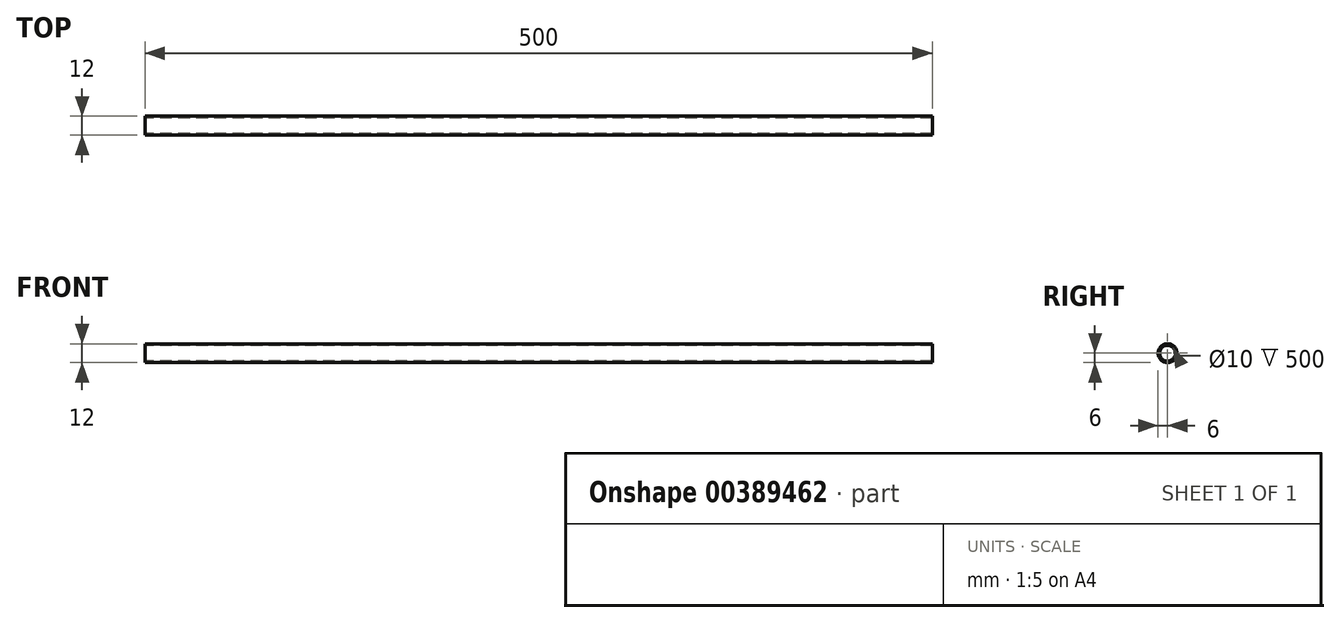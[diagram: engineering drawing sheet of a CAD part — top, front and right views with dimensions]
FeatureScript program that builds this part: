
annotation { "Feature Type Name" : "Feature", "Feature Type Description" : "" }
export const myFeature = defineFeature(function(context is Context, id is Id, definition is map)
    precondition{}
    {
        {
            var Q0;
            Q0=qCreatedBy(makeId("Front.planeOp"),FACE);
            var sketch = newSketch(context, id + "F0", { "sketchPlane" : qUnion([Q0])});
            skLineSegment(sketch, "E0", {"start": v(-228.56, 0) * mm, "end": v(271.44, 0) * mm, "construction": true});
            skLineSegment(sketch, "E1", {"start": v(-228.56, 0) * mm, "end": v(-228.56, 6) * mm});
            skLineSegment(sketch, "E2", {"start": v(-228.56, 6) * mm, "end": v(-228.56, 6) * mm});
            skLineSegment(sketch, "E3", {"start": v(271.44, 6) * mm, "end": v(-228.56, 6) * mm});
            skLineSegment(sketch, "E4", {"start": v(271.44, 0) * mm, "end": v(271.44, 6) * mm});
            skLineSegment(sketch, "E5", {"start": v(-228.56, 5) * mm, "end": v(271.44, 5) * mm});
            skSolve(sketch);
        }
        {
            var Q0;
            Q0 = qSketchRegion(id + "F0", true);
            var Q1;
            Q1=sQuery(id+"F0.wireOp",EDGE,"E0");
            revolve(context, id + "F1", {"surfaceOperationType" : NewSurfaceOperationType.NEW, "entities" : qUnion([Q0]), "axis" : qUnion([Q1]), "revolveType" : RevolveType.FULL});
        }
    });
